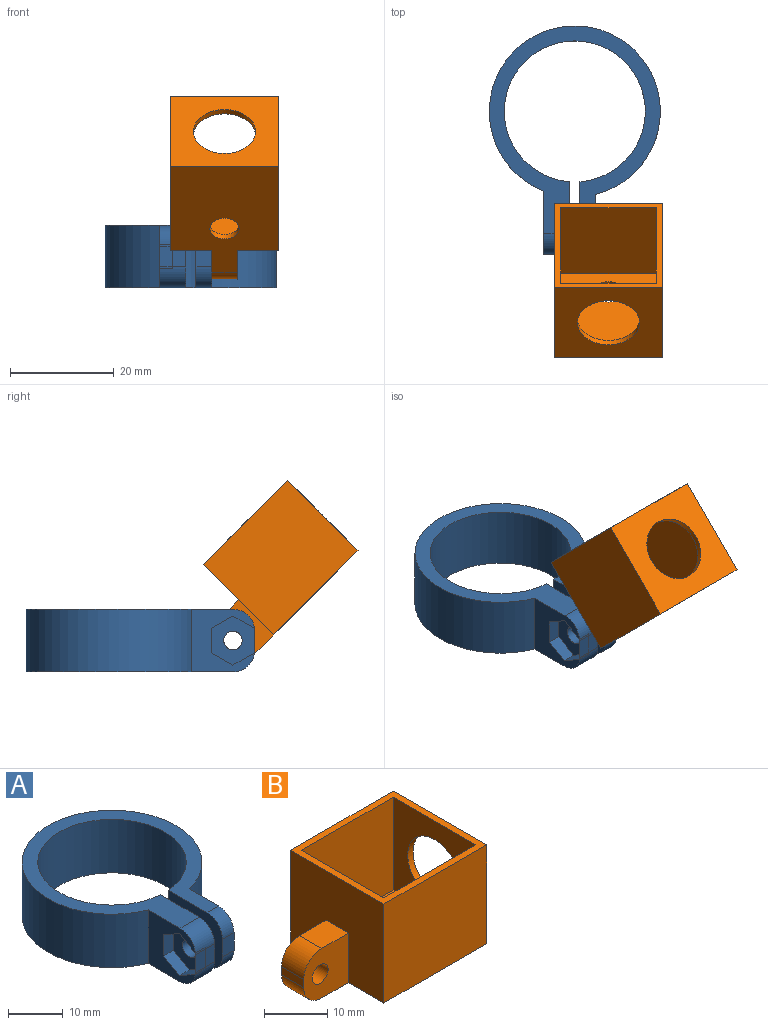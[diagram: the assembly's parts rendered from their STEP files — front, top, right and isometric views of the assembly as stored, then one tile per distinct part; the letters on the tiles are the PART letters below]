
ASSEMBLY  parts=2 mates=1
PART A: 23 faces, bbox 33x44.1x12 mm
  f0: plane 12.23x12mm, normal (-1,0,0), area 81.7mm2, adj f2,f7,f8,f10,f13,f14,f15,f16
  f1: cylinder r=1.78mm len=3.56mm, axis (1,0,0), area 27.5mm2, adj f3,f12
  f2: plane 40.1x33mm, normal (0,0,-1), area 328.1mm2, adj f0,f3,f4,f6,f7,f9,f19,f20
  f3: plane 14.04x12mm, normal (1,0,0), area 151.6mm2, adj f1,f2,f8,f9,f10,f19,f21
  f4: plane 14.04x12mm, normal (-1,0,0), area 151.6mm2, adj f2,f5,f9,f10,f11,f20,f22
  f5: plane 4x3mm, normal (0,-1,0), area 12mm2, adj f4,f6,f20,f22
  f6: plane 12x11.59mm, normal (1,0,0), area 122.3mm2, adj f2,f5,f7,f10,f11,f20,f22
  f7: cylinder r=16.5mm len=33mm, axis (0,0,-1), area 1121.9mm2, adj f0,f2,f6,f10
  f8: plane 5x4mm, normal (0,-1,0), area 20mm2, adj f0,f3,f19,f21
  f9: cylinder r=13.6mm len=27.2mm, axis (0,0,-1), area 1001.4mm2, adj f2,f3,f4,f10
  f10: plane 40.1x33mm, normal (0,0,1), area 328.1mm2, adj f0,f3,f4,f6,f7,f9,f21,f22
  f11: cylinder r=1.78mm len=3.56mm, axis (1,0,0), area 33.5mm2, adj f4,f6
  f12: plane 9.47x8.2mm, normal (-1,0,0), area 48.3mm2, adj f1,f13,f14,f15,f16,f17,f18
  f13: plane 4.1x2.54mm, normal (0,0.5,-0.87), area 12mm2, adj f0,f12,f14,f18
  f14: plane 4.1x2.54mm, normal (0,-0.5,-0.87), area 12mm2, adj f0,f12,f13,f15
  f15: plane 4.73x2.54mm, normal (0,-1,0), area 12mm2, adj f0,f12,f14,f16
  f16: plane 4.1x2.54mm, normal (0,-0.5,0.87), area 12mm2, adj f0,f12,f15,f17
  f17: plane 4.1x2.54mm, normal (0,0.5,0.87), area 12mm2, adj f0,f12,f16,f18
  f18: plane 4.73x2.54mm, normal (0,1,0), area 12mm2, adj f0,f12,f13,f17
  f19: cylinder r=4mm len=5mm, axis (1,0,0), area 31.4mm2, adj f0,f2,f3,f8
  f20: cylinder r=4mm len=4mm, axis (1,0,0), area 18.8mm2, adj f2,f4,f5,f6
  f21: cylinder r=4mm len=5mm, axis (-1,0,0), area 31.4mm2, adj f0,f3,f8,f10
  f22: cylinder r=4mm len=4mm, axis (-1,0,0), area 18.8mm2, adj f4,f5,f6,f10
PART B: 20 faces, bbox 33x20.9x19.2 mm
  f0: plane 23x20.9mm, normal (0,0,1), area 99.6mm2, adj f1,f3,f4,f5,f6,f8,f9,f10
  f1: plane 23x19.2mm, normal (0,-1,0), area 441.6mm2, adj f0,f2,f4,f5
  f2: plane 29x20.9mm, normal (0,0,-1), area 485.8mm2, adj f1,f3,f4,f5,f12,f14,f15,f18
  f3: plane 23x19.2mm, normal (0,1,0), area 441.6mm2, adj f0,f2,f4,f5
  f4: plane 20.9x19.2mm, normal (1,0,0), area 288.2mm2, adj f0,f1,f2,f3,f11
  f5: plane 20.9x19.2mm, normal (-1,0,0), area 353.3mm2, adj f0,f1,f2,f3,f13,f14,f15
  f6: plane 20.6x18mm, normal (0,1,0), area 370.8mm2, adj f0,f7,f9,f10
  f7: plane 20.6x18.5mm, normal (0,0,1), area 356.2mm2, adj f6,f8,f9,f10,f12
  f8: plane 20.6x18mm, normal (0,-1,0), area 370.8mm2, adj f0,f7,f9,f10
  f9: plane 18.5x18mm, normal (-1,0,0), area 219.9mm2, adj f0,f6,f7,f8,f11
  f10: plane 18.5x18mm, normal (1,0,0), area 333mm2, adj f0,f6,f7,f8
  f11: cylinder r=6mm len=12mm, axis (1,0,0), area 45.2mm2, adj f4,f9
  f12: cylinder r=2.81mm len=5.63mm, axis (0,0,-1), area 21.2mm2, adj f2,f7
  f13: plane 6x5mm, normal (0,0,1), area 30mm2, adj f5,f14,f15,f19
  f14: plane 10x9.6mm, normal (0,1,0), area 79.2mm2, adj f2,f5,f13,f16,f17,f18,f19
  f15: plane 10x9.6mm, normal (0,-1,0), area 79.2mm2, adj f2,f5,f13,f16,f17,f18,f19
  f16: plane 5x1.6mm, normal (-1,0,0), area 8mm2, adj f14,f15,f18,f19
  f17: cylinder r=1.78mm len=5mm, axis (0,-1,0), area 55.9mm2, adj f14,f15
  f18: cylinder r=4mm len=5mm, axis (0,-1,0), area 31.4mm2, adj f2,f14,f15,f16
  f19: cylinder r=4mm len=5mm, axis (0,-1,0), area 31.4mm2, adj f13,f14,f15,f16
PLACE A t=(4.45,9.59,0.16)mm
PLACE B rot(axis=(-0.36,-0.36,-0.86),98.4deg) t=(14.47,-30.58,-1.6)mm
MATE revolute B.f17 <-> A.f1  axis (-1,0,0) through (8.45,-13.86,6.16)mm
